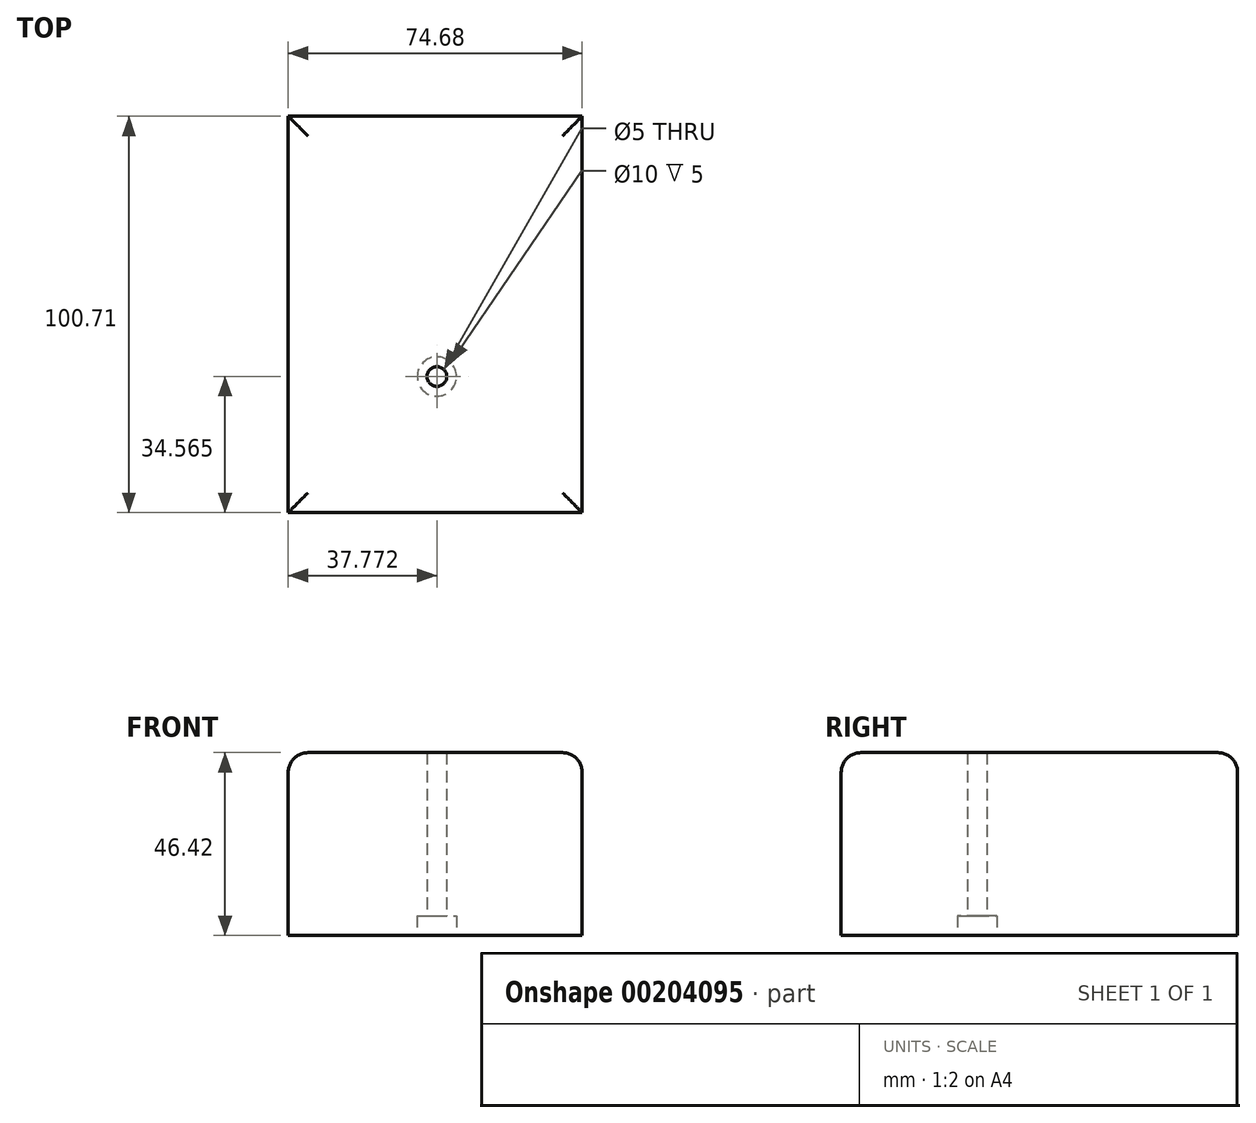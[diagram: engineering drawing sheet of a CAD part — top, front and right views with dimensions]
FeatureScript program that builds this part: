
annotation { "Feature Type Name" : "Feature", "Feature Type Description" : "" }
export const myFeature = defineFeature(function(context is Context, id is Id, definition is map)
    precondition{}
    {
        {
            var Q0;
            Q0=qCreatedBy(makeId("Front.planeOp"),FACE);
            var sketch = newSketch(context, id + "F3", { "sketchPlane" : qUnion([Q0])});
            skLineSegment(sketch, "E0.bottom", {"start": v(0, 0) * mm, "end": v(74.68, 0) * mm});
            skLineSegment(sketch, "E0.top", {"start": v(0, 46.42) * mm, "end": v(74.68, 46.42) * mm});
            skLineSegment(sketch, "E0.left", {"start": v(0, 0) * mm, "end": v(0, 46.42) * mm});
            skLineSegment(sketch, "E0.right", {"start": v(74.68, 0) * mm, "end": v(74.68, 46.42) * mm});
            skSolve(sketch);
        }
        {
            var Q0;
            Q0=makeQuery(id+"F3.imprint","IMPRINT",FACE,{"disambiguationData":[TD([[makeQuery(id+"F3.imprint","IMPRINT",EDGE,{"derivedFrom":sQuery(id+"F3.wireOp",EDGE,"E0.bottom")}),1.0]])]});
            extrude(context, id + "F0", {"entities" : qUnion([Q0]), "depth" : 100.7 * mm});
        }
        {
            var Q0;
            Q0=makeQuery(id+"F0.opExtrude","SWEPT_EDGE",EDGE,{"disambiguationData":[OSD([sQuery(id+"F3.wireOp",EDGE,"E0.top"),sQuery(id+"F3.wireOp",EDGE,"E0.right")])]});
            var Q1;
            Q1=makeQuery(id+"F0.opExtrude","CAP_EDGE",EDGE,{"disambiguationData":[OSD([sQuery(id+"F3.wireOp",EDGE,"E0.top")])],"isStart":false});
            var Q2;
            Q2=makeQuery(id+"F0.opExtrude","CAP_EDGE",EDGE,{"disambiguationData":[OSD([sQuery(id+"F3.wireOp",EDGE,"E0.top")])],"isStart":true});
            var Q3;
            Q3=makeQuery(id+"F0.opExtrude","SWEPT_EDGE",EDGE,{"disambiguationData":[OSD([sQuery(id+"F3.wireOp",EDGE,"E0.top"),sQuery(id+"F3.wireOp",EDGE,"E0.left")])]});
            fillet(context, id + "F1", {"entities" : qUnion([Q0, Q1, Q2, Q3]), "radius" : 5 * mm, "tangentPropagation" : true, "allowEdgeOverflow" : false});
        }
        {
            var Q0;
            Q0=makeQuery(id+"F0.opExtrude","SWEPT_FACE",FACE,{"disambiguationData":[OSD([sQuery(id+"F3.wireOp",EDGE,"E0.bottom")])]});
            var sketch = newSketch(context, id + "F4", { "sketchPlane" : qUnion([Q0])});
            skPoint(sketch, "E1", {"position": v(37.77, 66.14) * mm});
            skSolve(sketch);
        }
        {
            var Q0;
            Q0=sQuery(id+"F4.wireOp",VERTEX,"E1");
            var Q1;
            Q1=makeQuery(id+"F0.opExtrude","SWEPT_BODY",BODY,{"disambiguationData":[OSD([sQuery(id+"F3.wireOp",EDGE,"E0.bottom"),sQuery(id+"F3.wireOp",EDGE,"E0.top"),sQuery(id+"F3.wireOp",EDGE,"E0.left"),sQuery(id+"F3.wireOp",EDGE,"E0.right")])]});
            hole(context, id + "F2", {"style" : HoleStyle.C_BORE, "endStyle" : HoleEndStyle.THROUGH, "holeDiameter" : 5 * mm, "cBoreDiameter" : 10 * mm, "cBoreDepth" : 5 * mm, "locations" : qUnion([Q0]), "scope" : qUnion([Q1]), "isTappedThrough" : true});
        }
    });
